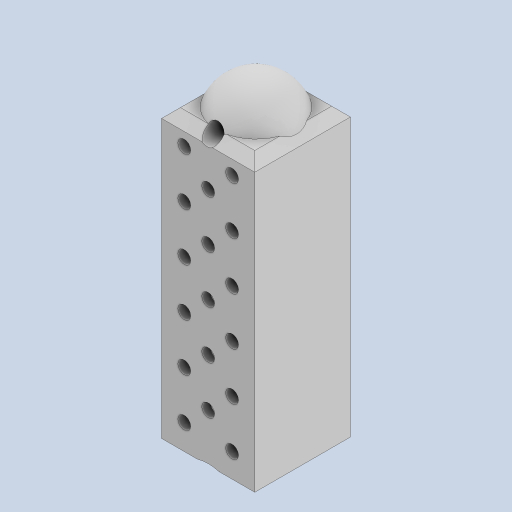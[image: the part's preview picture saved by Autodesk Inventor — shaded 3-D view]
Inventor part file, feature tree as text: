
AUTODESK INVENTOR PART (.ipt)
format: ipt  version: 2024 (Build 280153000, 153)  size: 523,776 bytes
history: native  units: mm
features: sketch x11, extrude x10, projected_geometry x9, plane x2, mirror x2, chamfer x2, revolve x1
ambient origin geometry x8: Origin, YZ Plane, XZ Plane, XY Plane, X Axis, Y Axis, Z Axis, Center Point
bodies: Solid1 (feature_tree)
feature tree (37):
  extrude  "Extrusion1"  Depth=50.8mm
  extrude  "Extrusion2"  Depth=26.5mm
  extrude  "Extrusion3"  Depth=25.4mm
  extrude  "Extrusion4"  Depth=29.5mm
  extrude  "Extrusion7"  Depth=29.5mm
  plane  "Work Plane1"
  extrude  "Extrusion13"  Depth=70.75mm TaperAngle=0.0deg
  mirror  "Mirror3"
  revolve  "Revolution1"  [1 undecoded]
  extrude  "Extrusion8"  TaperAngle=0.0deg  [1 undecoded]
  extrude  "Extrusion10"  Depth=6.85mm
  mirror  "Mirror2"
  chamfer  "Chamfer1"  Distance=25.4mm
  plane  "Work Plane2"
  extrude  "Extrusion12"  Depth=10.0mm
  chamfer  "Chamfer2"  [1 undecoded]
  extrude  "Extrusion14"  Depth=10.0mm
  sketch  "Sketch1"  dims[d0=49.5mm d1=50.8mm]
  sketch  "Sketch2"  dims[d2=26.5mm d3=26.5mm]
  projected_geometry  "Projected Loop1"
  sketch  "Sketch3"  dims[d4=26.5mm d7=25.4mm]
  projected_geometry  "Projected Loop2"
  sketch  "Sketch4"  dims[d8=29.5mm d9=29.5mm]
  projected_geometry  "Projected Loop3"
  sketch  "Sketch7"  dims[d10=29.5mm d12=24.75mm]
  projected_geometry  "Projected Loop6"
  sketch  "Sketch8"  dims[d14=80.0mm d15=0.0mm d16=70.75mm d17=0.0mm]
  projected_geometry  "Projected Loop7"
  sketch  "Sketch9"  dims[d18=1.5mm d19=0.0mm d20=3.0mm]
  projected_geometry  "Projected Loop8"
  sketch  "Sketch11"  dims[d21=50.5mm d22=25.25mm d23=0.0mm d24=0.0mm]
  sketch  "Sketch13"  dims[d30=6.85mm d31=6.85mm]
  projected_geometry  "Projected Loop10"
  sketch  "Sketch14"  dims[d32=6.85mm]
  projected_geometry  "Projected Loop11"
  sketch  "Sketch15"  dims[d33=12.7mm d34=25.4mm d35=25.4mm d36=0.0mm d37=12.7mm d38=80.0mm d40=25.4mm d41=10.0mm d43=10.0mm d45=10.0mm d46=0.0mm d47=-24.75mm d48=49.5mm d49=15.0mm d52=5.0mm d53=10.0mm d54=360.0deg d55=8.5mm d56=12.5mm d57=22.5mm d58=5.0mm d59=9.0mm d60=13.5mm d61=0.0mm d65=3.0mm d66=25.4mm d67=0.0mm d68=5.0mm d69=2.0mm d70=45.0deg d71=29.5mm d72=14.75mm d73=0.0mm d74=0.0mm d75=0.0mm d76=17.0mm d79=1.5mm d80=0.0mm d82=6.5mm d83=6.5mm d84=0.0mm d86=-90.0mm d87=0.0mm d88=0.0mm d89=50.8mm d90=49.5mm d91=30.8mm d92=29.5mm d93=45.0mm d94=0.0mm d95=5.0mm d96=2.0mm d97=45.0deg d98=2.75mm d99=2.75mm d100=2.75mm d101=12.7mm d102=25.4mm d103=12.7mm d104=12.7mm d105=0.0mm d106=70.0mm d108=25.4mm d109=10.0mm d111=10.0mm d113=15.0mm d114=0.0mm d115=6.85mm d116=6.85mm d117=6.85mm d118=60.0mm d120=25.4mm d121=10.0mm d123=10.0mm d125=15.0mm d126=0.0mm d81=0.5mm]
  projected_geometry  "Projected Loop12"
note: 3 required parameter values undecoded (feature->parameter linkage not recoverable at this tier; creation-order binding heuristic only, values carry confidence <= 0.55)